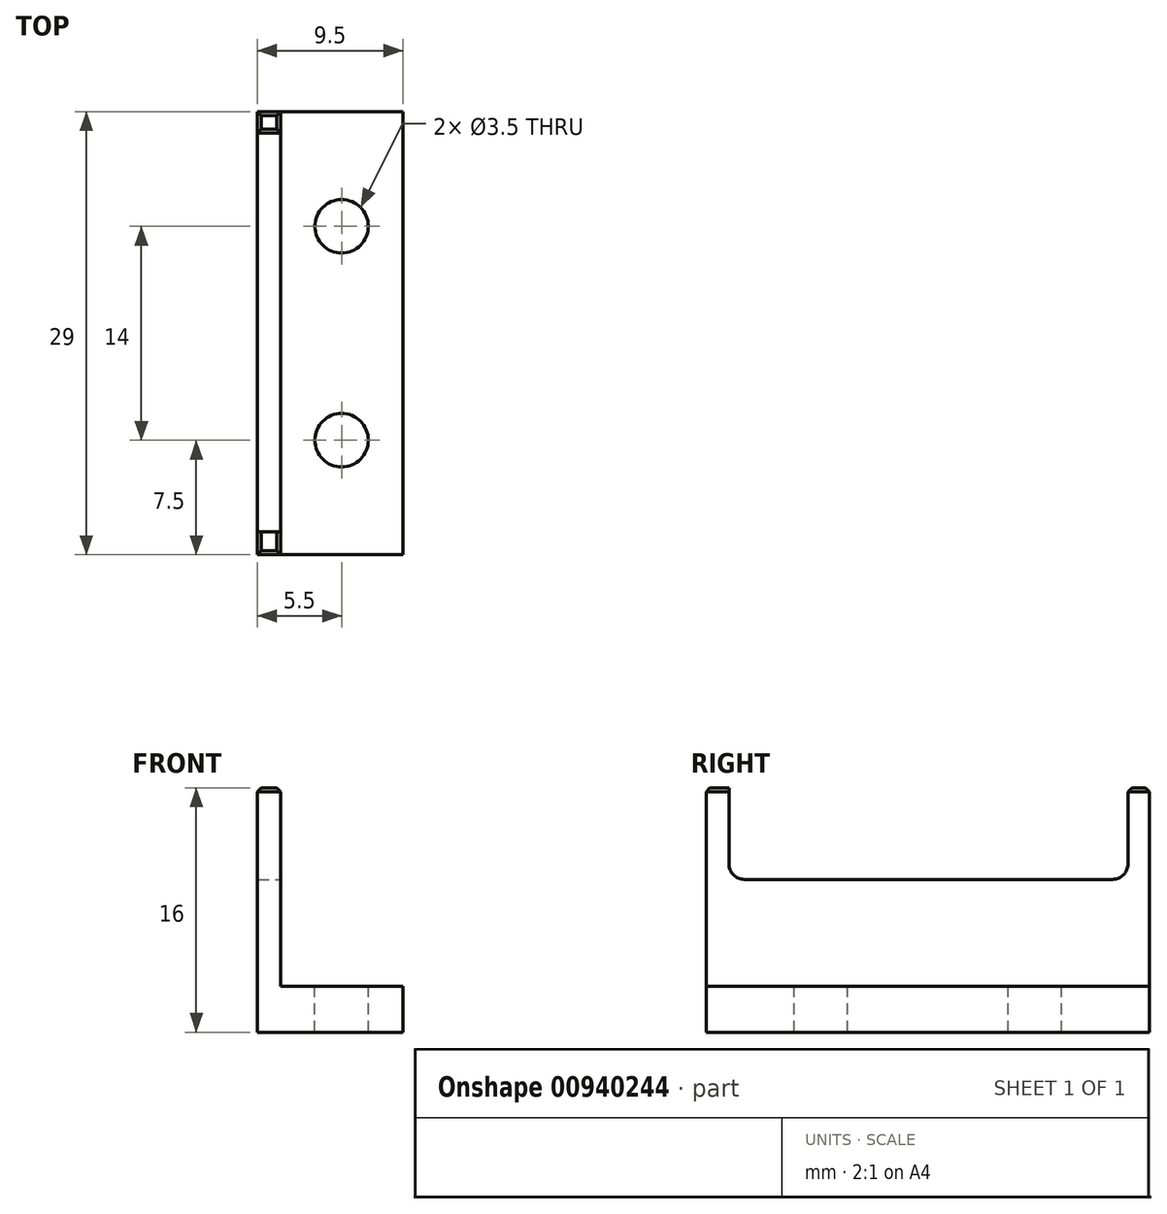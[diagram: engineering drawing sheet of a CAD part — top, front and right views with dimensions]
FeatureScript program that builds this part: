
annotation { "Feature Type Name" : "Feature", "Feature Type Description" : "" }
export const myFeature = defineFeature(function(context is Context, id is Id, definition is map)
    precondition{}
    {
        {
            var Q0;
            Q0=qCreatedBy(makeId("Top.planeOp"),FACE);
            var sketch = newSketch(context, id + "F0", { "sketchPlane" : qUnion([Q0])});
            skLineSegment(sketch, "E0", {"start": v(0, 0) * mm, "end": v(0, 29) * mm});
            skLineSegment(sketch, "E1", {"start": v(0, 29) * mm, "end": v(9.5, 29) * mm});
            skLineSegment(sketch, "E2", {"start": v(9.5, 29) * mm, "end": v(9.5, 0) * mm});
            skLineSegment(sketch, "E3", {"start": v(9.5, 0) * mm, "end": v(0, 0) * mm});
            skLineSegment(sketch, "E4", {"start": v(0, 29) * mm, "end": v(1.5, 29) * mm});
            skSolve(sketch);
        }
        {
            var Q0;
            Q0=makeQuery(id+"F0.imprint","IMPRINT",FACE,{"disambiguationData":[TD([[makeQuery(id+"F0.imprint","IMPRINT",EDGE,{"derivedFrom":sQuery(id+"F0.wireOp",EDGE,"E0")}),-1.0]])]});
            extrude(context, id + "F1", {"entities" : qUnion([Q0]), "depth" : 3 * mm, "offsetDistance" : 25 * mm});
        }
        {
            var Q0;
            Q0=makeQuery(id+"F1.opExtrude","CAP_FACE",FACE,{"disambiguationData":[OSD([sQuery(id+"F0.wireOp",EDGE,"E0"),sQuery(id+"F0.wireOp",EDGE,"E1"),sQuery(id+"F0.wireOp",EDGE,"E2"),sQuery(id+"F0.wireOp",EDGE,"E3"),sQuery(id+"F0.wireOp",EDGE,"E4")])],"isStart":false});
            var sketch = newSketch(context, id + "F2", { "sketchPlane" : qUnion([Q0])});
            skLineSegment(sketch, "E5", {"start": v(0, 29) * mm, "end": v(1.5, 29) * mm});
            skLineSegment(sketch, "E6", {"start": v(1.5, 29) * mm, "end": v(1.5, 0) * mm});
            skLineSegment(sketch, "E7", {"start": v(1.5, 0) * mm, "end": v(0, 0) * mm});
            skSolve(sketch);
        }
        {
            var Q0;
            Q0=makeQuery(id+"F2.imprint","IMPRINT",FACE,{"disambiguationData":[TD([[makeQuery(id+"F2.imprint","IMPRINT",EDGE,{"derivedFrom":sQuery(id+"F2.wireOp",EDGE,"E5")}),-1.0]])]});
            extrude(context, id + "F3", {"entities" : qUnion([Q0]), "operationType" : NewBodyOperationType.ADD, "depth" : 13 * mm, "offsetDistance" : 25 * mm});
        }
        {
            var Q0;
            Q0=makeQuery(id+"F1.opExtrude","CAP_FACE",FACE,{"disambiguationData":[OSD([sQuery(id+"F0.wireOp",EDGE,"E0"),sQuery(id+"F0.wireOp",EDGE,"E1"),sQuery(id+"F0.wireOp",EDGE,"E2"),sQuery(id+"F0.wireOp",EDGE,"E3"),sQuery(id+"F0.wireOp",EDGE,"E4")])],"isStart":false});
            var sketch = newSketch(context, id + "F4", { "sketchPlane" : qUnion([Q0])});
            skCircle(sketch, "E8", {"center": v(5.5, 21.5) * mm, "radius": 1.75 * mm});
            skCircle(sketch, "E9", {"center": v(5.5, 7.5) * mm, "radius": 1.75 * mm});
            skSolve(sketch);
        }
        {
            var Q0;
            Q0=sQuery(id+"F4.wireOp",VERTEX,"E8.center");
            var Q1;
            Q1=sQuery(id+"F4.wireOp",VERTEX,"E9.center");
            var Q2;
            Q2=makeQuery(id+"F1.opExtrude","SWEPT_BODY",BODY,{"disambiguationData":[OSD([sQuery(id+"F0.wireOp",EDGE,"E0"),sQuery(id+"F0.wireOp",EDGE,"E1"),sQuery(id+"F0.wireOp",EDGE,"E2"),sQuery(id+"F0.wireOp",EDGE,"E3"),sQuery(id+"F0.wireOp",EDGE,"E4")])]});
            hole(context, id + "F5", {"style" : HoleStyle.SIMPLE, "endStyle" : HoleEndStyle.THROUGH, "holeDiameter" : 3.5 * mm, "majorDiameter" : 5 * mm, "tappedDepth" : 10 * mm, "tapClearance" : 3, "locations" : qUnion([Q0, Q1]), "scope" : qUnion([Q2])});
        }
        {
            var Q0;
            Q0=makeQuery(id+"F3.opExtrude","SWEPT_FACE",FACE,{"disambiguationData":[OSD([sQuery(id+"F2.wireOp",EDGE,"E6")])]});
            var sketch = newSketch(context, id + "F6", { "sketchPlane" : qUnion([Q0])});
            skLineSegment(sketch, "E10", {"start": v(0, 16) * mm, "end": v(1.5, 16) * mm});
            skLineSegment(sketch, "E11", {"start": v(29, 16) * mm, "end": v(27.5, 16) * mm});
            skLineSegment(sketch, "E12.bottom", {"start": v(1.5, 16) * mm, "end": v(27.6, 16) * mm});
            skLineSegment(sketch, "E12.top", {"start": v(1.5, 10) * mm, "end": v(27.6, 10) * mm});
            skLineSegment(sketch, "E12.left", {"start": v(1.5, 16) * mm, "end": v(1.5, 10) * mm});
            skLineSegment(sketch, "E12.right", {"start": v(27.6, 16) * mm, "end": v(27.6, 10) * mm});
            skSolve(sketch);
        }
        {
            var Q0;
            Q0=makeQuery(id+"F6.imprint","IMPRINT",FACE,{"disambiguationData":[TD([[makeQuery(id+"F6.imprint","IMPRINT",EDGE,{"derivedFrom":sQuery(id+"F6.wireOp",EDGE,"E12.top")}),1.0]])]});
            extrude(context, id + "F7", {"entities" : qUnion([Q0]), "operationType" : NewBodyOperationType.REMOVE, "endBound" : BoundingType.THROUGH_ALL, "oppositeDirection" : true, "depth" : 25 * mm, "offsetDistance" : 25 * mm});
        }
        {
            var Q0;
            Q0=makeQuery(id+"F7.boolean.opBoolean","COPY",EDGE,{"derivedFrom":makeQuery(id+"F7.opExtrude","SWEPT_EDGE",EDGE,{"disambiguationData":[OSD([sQuery(id+"F6.wireOp",EDGE,"E12.top"),sQuery(id+"F6.wireOp",EDGE,"E12.right")])]})});
            var Q1;
            Q1=makeQuery(id+"F7.boolean.opBoolean","COPY",EDGE,{"derivedFrom":makeQuery(id+"F7.opExtrude","SWEPT_EDGE",EDGE,{"disambiguationData":[OSD([sQuery(id+"F6.wireOp",EDGE,"E12.top"),sQuery(id+"F6.wireOp",EDGE,"E12.left")])]})});
            fillet(context, id + "F8", {"entities" : qUnion([Q0, Q1]), "radius" : 1 * mm, "tangentPropagation" : true, "allowEdgeOverflow" : false});
        }
        {
            var Q0;
            Q0=makeQuery(id+"F7.boolean.opBoolean","COPY",EDGE,{"derivedFrom":makeQuery(id+"F7.opExtrude","SWEPT_EDGE",EDGE,{"disambiguationData":[OSD([sQuery(id+"F6.wireOp",EDGE,"E11"),sQuery(id+"F6.wireOp",EDGE,"E12.bottom"),sQuery(id+"F6.wireOp",EDGE,"E12.right")])]})});
            var Q1;
            {var subQ0=sQuery(id+"F2.wireOp",EDGE,"E6");var subQ1=sQuery(id+"F2.wireOp",EDGE,"E5");Q1=makeQuery(id+"F7.boolean.opBoolean","SPLIT",EDGE,{"disambiguationData":[TD([makeQuery(id+"F3.opExtrude","SWEPT_FACE",FACE,{"disambiguationData":[OSD([subQ1])]})])],"derivedFrom":makeQuery(id+"F3.opExtrude","CAP_EDGE",EDGE,{"disambiguationData":[OSD([subQ0])],"isStart":false})});}
            var Q2;
            Q2=makeQuery(id+"F3.opExtrude","CAP_EDGE",EDGE,{"disambiguationData":[OSD([sQuery(id+"F2.wireOp",EDGE,"E5")])],"isStart":false});
            var Q3;
            {var subQ0=sQuery(id+"F2.wireOp",EDGE,"E5");var subQ1=sQuery(id+"F0.wireOp",EDGE,"E0");Q3=makeQuery(id+"F7.boolean.opBoolean","SPLIT",EDGE,{"disambiguationData":[TD([makeQuery(id+"F3.opExtrude","SWEPT_FACE",FACE,{"disambiguationData":[OSD([subQ0])]})])],"derivedFrom":makeQuery(id+"F3.opExtrude","CAP_EDGE",EDGE,{"disambiguationData":[OSD([subQ1])],"isStart":false})});}
            var Q4;
            Q4=makeQuery(id+"F7.boolean.opBoolean","COPY",EDGE,{"derivedFrom":makeQuery(id+"F7.opExtrude","SWEPT_EDGE",EDGE,{"disambiguationData":[OSD([sQuery(id+"F6.wireOp",EDGE,"E10"),sQuery(id+"F6.wireOp",EDGE,"E12.bottom"),sQuery(id+"F6.wireOp",EDGE,"E12.left")])]})});
            var Q5;
            {var subQ1=sQuery(id+"F2.wireOp",EDGE,"E6");Q5=makeQuery(id+"F7.boolean.opBoolean","SPLIT",EDGE,{"disambiguationData":[TD([makeQuery(id+"F1.opExtrude","SWEPT_FACE",FACE,{"disambiguationData":[OSD([sQuery(id+"F0.wireOp",EDGE,"E3")])]})])],"derivedFrom":makeQuery(id+"F3.opExtrude","CAP_EDGE",EDGE,{"disambiguationData":[OSD([subQ1])],"isStart":false})});}
            var Q6;
            Q6=makeQuery(id+"F3.opExtrude","CAP_EDGE",EDGE,{"disambiguationData":[OSD([sQuery(id+"F2.wireOp",EDGE,"E7")])],"isStart":false});
            var Q7;
            {var subQ1=sQuery(id+"F0.wireOp",EDGE,"E0");Q7=makeQuery(id+"F7.boolean.opBoolean","SPLIT",EDGE,{"disambiguationData":[TD([makeQuery(id+"F1.opExtrude","SWEPT_FACE",FACE,{"disambiguationData":[OSD([sQuery(id+"F0.wireOp",EDGE,"E3")])]})])],"derivedFrom":makeQuery(id+"F3.opExtrude","CAP_EDGE",EDGE,{"disambiguationData":[OSD([subQ1])],"isStart":false})});}
            chamfer(context, id + "F9", {"entities" : qUnion([Q0, Q1, Q2, Q3, Q4, Q5, Q6, Q7]), "width" : 0.25 * mm, "tangentPropagation" : true});
        }
    });
